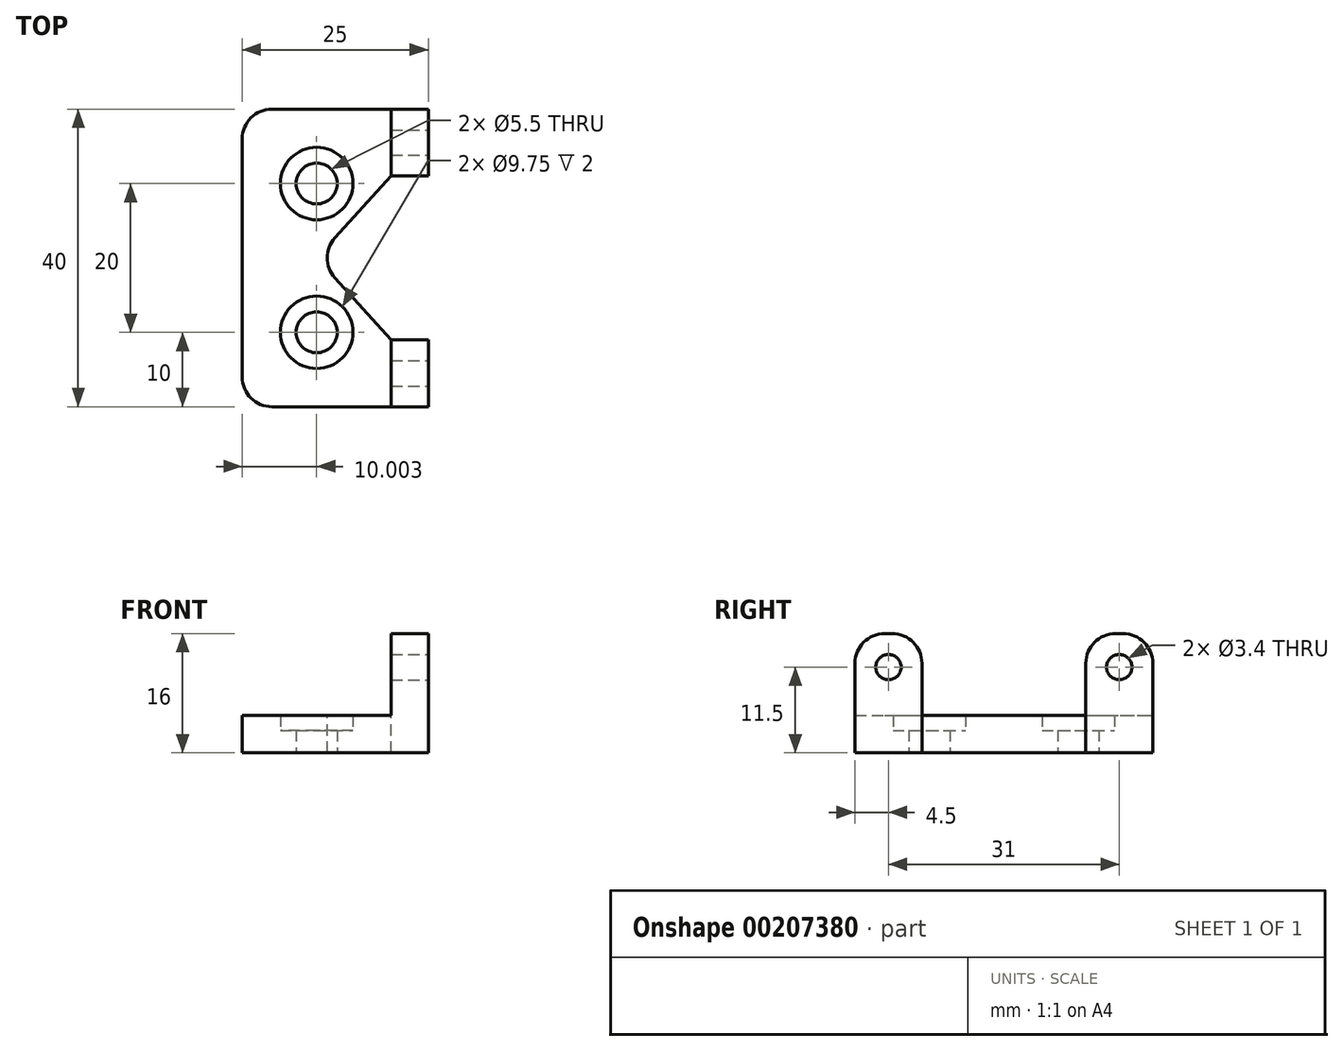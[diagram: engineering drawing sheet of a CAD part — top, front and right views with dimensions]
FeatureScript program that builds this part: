
annotation { "Feature Type Name" : "Feature", "Feature Type Description" : "" }
export const myFeature = defineFeature(function(context is Context, id is Id, definition is map)
    precondition{}
    {
        {
            var Q0;
            Q0=qCreatedBy(makeId("Top.planeOp"),FACE);
            var sketch = newSketch(context, id + "F0", { "sketchPlane" : qUnion([Q0])});
            skLineSegment(sketch, "E0.bottom", {"start": v(-42.6, -40) * mm, "end": v(-53.6, -40) * mm});
            skLineSegment(sketch, "E0.top", {"start": v(-42.6, 0) * mm, "end": v(-53.6, 0) * mm});
            skLineSegment(sketch, "E0.right", {"start": v(-53.6, -40) * mm, "end": v(-53.6, 0) * mm});
            skCircle(sketch, "E1", {"center": v(-47.1, -4.5) * mm, "radius": 1.7 * mm});
            skCircle(sketch, "E2", {"center": v(-47.1, -35.5) * mm, "radius": 1.7 * mm});
            skLineSegment(sketch, "E3", {"start": v(-47.1, -4.5) * mm, "end": v(-16.1, -35.5) * mm, "construction": true});
            skArc(sketch, "E4", {"start": v(-42.6, -15.2) * mm, "mid": v(-43.6, -20) * mm, "end": v(-42.6, -24.8) * mm});
            skLineSegment(sketch, "E5", {"start": v(-53.6, 0) * mm, "end": v(-58.6, 0) * mm});
            skLineSegment(sketch, "E6", {"start": v(-58.6, 0) * mm, "end": v(-58.6, -40) * mm});
            skLineSegment(sketch, "E7", {"start": v(-58.6, -40) * mm, "end": v(-53.6, -40) * mm});
            skLineSegment(sketch, "E8", {"start": v(-42.6, 0) * mm, "end": v(-42.6, -40) * mm});
            skPoint(sketch, "E9.center.orphan", {"position": v(-16.1, -4.5) * mm});
            skLineSegment(sketch, "E10", {"start": v(-42.6, -9) * mm, "end": v(-53.6, -9) * mm});
            skLineSegment(sketch, "E11", {"start": v(-42.6, -31) * mm, "end": v(-53.6, -31) * mm});
            skSolve(sketch);
        }
        {
            var Q0;
            {var subQ1=sQuery(id+"F0.wireOp",EDGE,"9c0b02a7-613c-446a-83a0-19864fdcf40f");Q0=makeQuery(id+"F0.imprint","IMPRINT",FACE,{"disambiguationData":[TD([[makeQuery(id+"F0.imprint","IMPRINT",EDGE,{"derivedFrom":subQ1}),1.0]])]});}
            var Q1;
            {var subQ5=sQuery(id+"F0.wireOp",EDGE,"E0.bottom");Q1=makeQuery(id+"F0.imprint","IMPRINT",FACE,{"disambiguationData":[TD([[makeQuery(id+"F0.imprint","IMPRINT",EDGE,{"derivedFrom":subQ5}),-1.0]])]});}
            var Q2;
            {var subQ1=sQuery(id+"F0.wireOp",EDGE,"E0.top");Q2=makeQuery(id+"F0.imprint","IMPRINT",FACE,{"disambiguationData":[TD([[makeQuery(id+"F0.imprint","IMPRINT",EDGE,{"derivedFrom":subQ1}),1.0]])]});}
            extrude(context, id + "F1", {"entities" : qUnion([Q0, Q1, Q2]), "depth" : 5 * mm, "offsetDistance" : 25 * mm});
        }
        {
            var Q0;
            Q0=makeQuery(id+"F0.imprint","IMPRINT",FACE,{"disambiguationData":[TD([[makeQuery(id+"F0.imprint","IMPRINT",EDGE,{"derivedFrom":sQuery(id+"F0.wireOp",EDGE,"E0.right")}),1.0]])]});
            extrude(context, id + "F2", {"entities" : qUnion([Q0]), "operationType" : NewBodyOperationType.ADD, "depth" : 25 * mm, "offsetDistance" : 25 * mm});
        }
        {
            var Q0;
            Q0=makeQuery(id+"F2.opExtrude","SWEPT_FACE",FACE,{"disambiguationData":[OSD([sQuery(id+"F0.wireOp",EDGE,"E0.right")])]});
            var sketch = newSketch(context, id + "F3", { "sketchPlane" : qUnion([Q0])});
            skPoint(sketch, "E12", {"position": v(-40, 15) * mm});
            skPoint(sketch, "E13", {"position": v(-30, 15) * mm});
            skPoint(sketch, "E14", {"position": v(-10, 15) * mm});
            skLineSegment(sketch, "E15", {"start": v(-30, 15) * mm, "end": v(-10, 15) * mm, "construction": true});
            skPoint(sketch, "E16", {"position": v(-20, 15) * mm});
            skPoint(sketch, "E17", {"position": v(-20, 25) * mm});
            skLineSegment(sketch, "E18", {"start": v(-31, 5) * mm, "end": v(-20, 15) * mm});
            skLineSegment(sketch, "E19", {"start": v(-9, 5) * mm, "end": v(-20, 15) * mm});
            skSolve(sketch);
        }
        {
            var Q0;
            Q0=sQuery(id+"F3.wireOp",VERTEX,"E14");
            var Q1;
            Q1=sQuery(id+"F3.wireOp",VERTEX,"E13");
            var Q2;
            Q2=makeQuery(id+"F1.opExtrude","SWEPT_BODY",BODY,{"disambiguationData":[OSD([sQuery(id+"F0.wireOp",EDGE,"E0.bottom"),sQuery(id+"F0.wireOp",EDGE,"E0.top"),sQuery(id+"F0.wireOp",EDGE,"E0.left"),sQuery(id+"F0.wireOp",EDGE,"E0.right"),sQuery(id+"F0.wireOp",EDGE,"E1"),sQuery(id+"F0.wireOp",EDGE,"E2"),sQuery(id+"F0.wireOp",EDGE,"2d8cc5c3-e3e5-4798-b1c8-c3ecc94b430d"),sQuery(id+"F0.wireOp",EDGE,"E4"),sQuery(id+"F0.wireOp",EDGE,"E9")])]});
            hole(context, id + "F4", {"style" : HoleStyle.C_BORE, "endStyle" : HoleEndStyle.THROUGH, "holeDiameter" : 5.5 * mm, "cBoreDiameter" : 9.75 * mm, "cBoreDepth" : 2 * mm, "majorDiameter" : 5 * mm, "isTappedThrough" : true, "tappedDepth" : 12 * mm, "tapClearance" : 3, "locations" : qUnion([Q0, Q1]), "scope" : qUnion([Q2]), "startStyle" : HoleStartStyle.PART});
        }
        {
            var Q0;
            Q0=makeQuery(id+"F3.imprint","IMPRINT",FACE,{"disambiguationData":[TD([[makeQuery(id+"F3.imprint","IMPRINT",EDGE,{"derivedFrom":sQuery(id+"F3.wireOp",EDGE,"E18")}),-1.0]])]});
            extrude(context, id + "F5", {"entities" : qUnion([Q0]), "operationType" : NewBodyOperationType.REMOVE, "endBound" : BoundingType.THROUGH_ALL, "oppositeDirection" : true, "depth" : 25 * mm, "offsetDistance" : 25 * mm});
        }
        {
            var Q0;
            Q0=makeQuery(id+"F1.opExtrude","SWEPT_EDGE",EDGE,{"disambiguationData":[OSD([sQuery(id+"F0.wireOp",EDGE,"E0.top"),sQuery(id+"F0.wireOp",EDGE,"E8")])]});
            var Q1;
            Q1=makeQuery(id+"F1.opExtrude","SWEPT_EDGE",EDGE,{"disambiguationData":[OSD([sQuery(id+"F0.wireOp",EDGE,"E0.bottom"),sQuery(id+"F0.wireOp",EDGE,"E8")])]});
            var Q2;
            Q2=makeQuery(id+"F2.opExtrude","CAP_EDGE",EDGE,{"disambiguationData":[OSD([sQuery(id+"F0.wireOp",EDGE,"E7")])],"isStart":false});
            var Q3;
            Q3=makeQuery(id+"F2.opExtrude","CAP_EDGE",EDGE,{"disambiguationData":[OSD([sQuery(id+"F0.wireOp",EDGE,"E5")])],"isStart":false});
            var Q4;
            Q4=makeQuery(id+"F1.opExtrude","SWEPT_EDGE",EDGE,{"disambiguationData":[OSD([sQuery(id+"F0.wireOp",EDGE,"E8"),sQuery(id+"F0.wireOp",EDGE,"E10")])]});
            var Q5;
            Q5=makeQuery(id+"F1.opExtrude","SWEPT_EDGE",EDGE,{"disambiguationData":[OSD([sQuery(id+"F0.wireOp",EDGE,"E8"),sQuery(id+"F0.wireOp",EDGE,"E11")])]});
            var Q6;
            Q6=makeQuery(id+"F5.boolean.opBoolean","COPY",EDGE,{"derivedFrom":makeQuery(id+"F5.opExtrude","SWEPT_EDGE",EDGE,{"disambiguationData":[OSD([sQuery(id+"F3.wireOp",EDGE,"E18"),sQuery(id+"F3.wireOp",EDGE,"E19")])]})});
            fillet(context, id + "F6", {"entities" : qUnion([Q0, Q1, Q2, Q3, Q4, Q5, Q6]), "radius" : 4 * mm, "tangentPropagation" : true, "allowEdgeOverflow" : false});
        }
        {
            var Q0;
            Q0=makeQuery(id+"F1.opExtrude","SWEPT_BODY",BODY,{"disambiguationData":[OSD([sQuery(id+"F0.wireOp",EDGE,"E0.bottom"),sQuery(id+"F0.wireOp",EDGE,"E0.right"),sQuery(id+"F0.wireOp",EDGE,"E2"),sQuery(id+"F0.wireOp",EDGE,"E8"),sQuery(id+"F0.wireOp",EDGE,"E11")])]});
            var Q1;
            Q1=sQuery(id+"F0.wireOp",EDGE,"E6");
            transform(context, id + "F7", {"entities" : qUnion([Q0]), "transformType" : TransformType.ROTATION, "transformAxis" : qUnion([Q1]), "angle" : 90 * degree, "makeCopy" : false});
        }
    });
